# Revit family: Recep. Victoria N.
name_source: partatom
category: Plumbing Fixtures
revit_build: Autodesk Revit 2015 (Build: 20140322_1515(x64)
units: mm (PartAtom-declared; Revit-internal decimal feet)

## types (1)
- Recep. Victoria N.
    Application = Shower
    Assembly Code = D2010.60
    BT_Color = Cromo
    BT_Itemizado_Estandar_CDT = H 06 06 00
    BT_Material = Cromo
    BT_SKU = 00 00 00
    BT_Uso = Baño
    Base Width = 215 mm
    Cold Water Connection = 13 mm
    Depth = 145 mm
    Description = Receptaculo Victoria-N
    Eco green certification = No
    Finish = Chrome
    Height = 1296 mm
    Hot Water Connection = 13 mm
    ID_Objeto = BT_F_F_1768
    ID_Source = BIMTOOL
    Installation type = Wall-mounted
    Keynote = 22 31 13
    Manufacturer = Roca
    Material Main = Cromo
    Model = Recep. Victoria N.
    Ref. No. = 5A2025C00
    Suitable for Children = No
    Suitable for Handicapped = No
    Supplier = Mk
    Type Comments = Mezclador de ducha externo de pared con flexible 1,50 mt, soporte movil de pared y ducha telefono
    URL = www.mk.cl
    Width = 306 mm

## geometry (parser evidence)
native form markers: Blend x6, Extrusion x2, Sweep x3
no freeform markers — native parametric forms only
